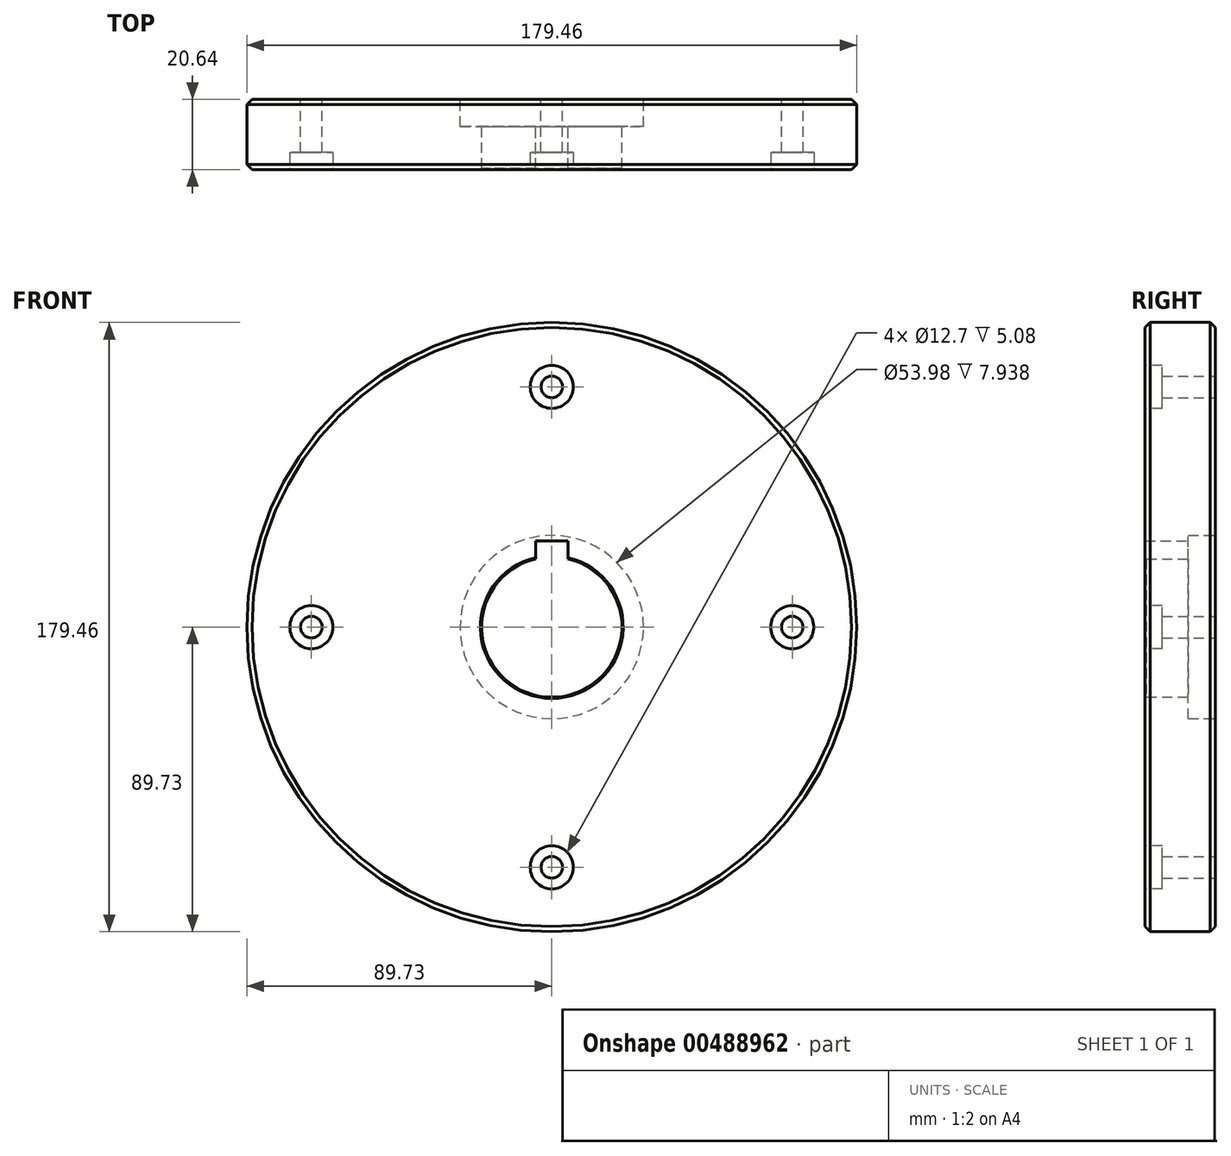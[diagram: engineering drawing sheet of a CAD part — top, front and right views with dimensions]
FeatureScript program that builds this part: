
annotation { "Feature Type Name" : "Feature", "Feature Type Description" : "" }
export const myFeature = defineFeature(function(context is Context, id is Id, definition is map)
    precondition{}
    {
        {
            var Q0;
            Q0=qCreatedBy(makeId("Front.planeOp"),FACE);
            var sketch = newSketch(context, id + "F0", { "sketchPlane" : qUnion([Q0])});
            skCircle(sketch, "E0", {"center": v(0, 0) * mm, "radius": 89.73 * mm});
            skArc(sketch, "E1", {"start": v(-4.76, 20.08) * mm, "mid": v(0, -20.64) * mm, "end": v(4.76, 20.08) * mm});
            skCircle(sketch, "E2", {"center": v(0, 0) * mm, "radius": 26.99 * mm});
            skLineSegment(sketch, "E3", {"start": v(-4.76, 20.08) * mm, "end": v(-4.76, 25.4) * mm});
            skLineSegment(sketch, "E4", {"start": v(-4.76, 25.4) * mm, "end": v(4.76, 25.4) * mm});
            skLineSegment(sketch, "E5", {"start": v(4.76, 25.4) * mm, "end": v(4.76, 20.08) * mm});
            skCircle(sketch, "E6", {"center": v(0, 0) * mm, "radius": 70.75 * mm, "construction": true});
            skCircle(sketch, "E7", {"center": v(0, 70.75) * mm, "radius": 3.18 * mm});
            skCircle(sketch, "E8.1.0", {"center": v(-70.75, 0) * mm, "radius": 3.18 * mm});
            skCircle(sketch, "E8.2.0", {"center": v(0, -70.75) * mm, "radius": 3.18 * mm});
            skCircle(sketch, "E8.3.0", {"center": v(70.75, 0) * mm, "radius": 3.18 * mm});
            skSolve(sketch);
        }
        {
            var Q0;
            Q0=makeQuery(id+"F0.imprint","IMPRINT",FACE,{"disambiguationData":[TD([[makeQuery(id+"F0.imprint","IMPRINT",EDGE,{"derivedFrom":sQuery(id+"F0.wireOp",EDGE,"E0")}),1.0]])]});
            var Q1;
            Q1=makeQuery(id+"F0.imprint","IMPRINT",FACE,{"disambiguationData":[TD([[makeQuery(id+"F0.imprint","IMPRINT",EDGE,{"derivedFrom":sQuery(id+"F0.wireOp",EDGE,"E1")}),-1.0]])]});
            extrude(context, id + "F1", {"entities" : qUnion([Q0, Q1]), "depth" : 20.64 * mm});
        }
        {
            var Q0;
            Q0=makeQuery(id+"F0.imprint","IMPRINT",FACE,{"disambiguationData":[TD([[makeQuery(id+"F0.imprint","IMPRINT",EDGE,{"derivedFrom":sQuery(id+"F0.wireOp",EDGE,"E1")}),-1.0]])]});
            extrude(context, id + "F2", {"entities" : qUnion([Q0]), "operationType" : NewBodyOperationType.REMOVE, "depth" : 7.94 * mm});
        }
        {
            var Q0;
            Q0=makeQuery(id+"F1.opExtrude","CAP_FACE",FACE,{"disambiguationData":[OSD([sQuery(id+"F0.wireOp",EDGE,"E0"),sQuery(id+"F0.wireOp",EDGE,"E1"),sQuery(id+"F0.wireOp",EDGE,"E3"),sQuery(id+"F0.wireOp",EDGE,"E4"),sQuery(id+"F0.wireOp",EDGE,"E5"),sQuery(id+"F0.wireOp",EDGE,"E7"),sQuery(id+"F0.wireOp",EDGE,"E8.1.0"),sQuery(id+"F0.wireOp",EDGE,"E8.2.0"),sQuery(id+"F0.wireOp",EDGE,"E8.3.0")])],"isStart":false});
            var sketch = newSketch(context, id + "F3", { "sketchPlane" : qUnion([Q0])});
            skCircle(sketch, "E9", {"center": v(0, 70.75) * mm, "radius": 6.35 * mm});
            skCircle(sketch, "E10.1.0", {"center": v(-70.75, 0) * mm, "radius": 6.35 * mm});
            skCircle(sketch, "E10.2.0", {"center": v(0, -70.75) * mm, "radius": 6.35 * mm});
            skCircle(sketch, "E10.3.0", {"center": v(70.75, 0) * mm, "radius": 6.35 * mm});
            skPoint(sketch, "E10.center", {"position": v(0, 0) * mm});
            skSolve(sketch);
        }
        {
            var Q0;
            Q0=makeQuery(id+"F3.imprint","IMPRINT",FACE,{"disambiguationData":[TD([[makeQuery(id+"F3.imprint","IMPRINT",EDGE,{"derivedFrom":sQuery(id+"F3.wireOp",EDGE,"E9")}),1.0]])]});
            var Q1;
            Q1=makeQuery(id+"F3.imprint","IMPRINT",FACE,{"disambiguationData":[TD([[makeQuery(id+"F3.imprint","IMPRINT",EDGE,{"derivedFrom":sQuery(id+"F3.wireOp",EDGE,"E10.1.0")}),1.0]])]});
            var Q2;
            Q2=makeQuery(id+"F3.imprint","IMPRINT",FACE,{"disambiguationData":[TD([[makeQuery(id+"F3.imprint","IMPRINT",EDGE,{"derivedFrom":sQuery(id+"F3.wireOp",EDGE,"E10.2.0")}),1.0]])]});
            var Q3;
            Q3=makeQuery(id+"F3.imprint","IMPRINT",FACE,{"disambiguationData":[TD([[makeQuery(id+"F3.imprint","IMPRINT",EDGE,{"derivedFrom":sQuery(id+"F3.wireOp",EDGE,"E10.3.0")}),1.0]])]});
            extrude(context, id + "F4", {"entities" : qUnion([Q0, Q1, Q2, Q3]), "operationType" : NewBodyOperationType.REMOVE, "oppositeDirection" : true, "depth" : 5.08 * mm});
        }
        {
            var Q0;
            Q0=makeQuery(id+"F1.opExtrude","SWEPT_FACE",FACE,{"disambiguationData":[OSD([sQuery(id+"F0.wireOp",EDGE,"E0")])]});
            chamfer(context, id + "F5", {"entities" : qUnion([Q0]), "width" : 1.52 * mm, "tangentPropagation" : true});
        }
        {
            var Q0;
            Q0=makeQuery(id+"F1.opExtrude","CAP_EDGE",EDGE,{"disambiguationData":[OSD([sQuery(id+"F0.wireOp",EDGE,"E1")])],"isStart":false});
            var Q1;
            Q1=makeQuery(id+"F4.boolean.opBoolean","COPY",EDGE,{"derivedFrom":makeQuery(id+"F4.opExtrude","CAP_EDGE",EDGE,{"disambiguationData":[OSD([sQuery(id+"F3.wireOp",EDGE,"E10.1.0")])],"isStart":true})});
            var Q2;
            Q2=makeQuery(id+"F4.boolean.opBoolean","COPY",EDGE,{"derivedFrom":makeQuery(id+"F4.opExtrude","CAP_EDGE",EDGE,{"disambiguationData":[OSD([sQuery(id+"F3.wireOp",EDGE,"E9")])],"isStart":true})});
            var Q3;
            Q3=makeQuery(id+"F4.boolean.opBoolean","COPY",EDGE,{"derivedFrom":makeQuery(id+"F4.opExtrude","CAP_EDGE",EDGE,{"disambiguationData":[OSD([sQuery(id+"F3.wireOp",EDGE,"E10.3.0")])],"isStart":true})});
            var Q4;
            Q4=makeQuery(id+"F4.boolean.opBoolean","COPY",EDGE,{"derivedFrom":makeQuery(id+"F4.opExtrude","CAP_EDGE",EDGE,{"disambiguationData":[OSD([sQuery(id+"F3.wireOp",EDGE,"E10.2.0")])],"isStart":true})});
            var Q5;
            Q5=makeQuery(id+"F2.boolean.opBoolean","COPY",EDGE,{"derivedFrom":makeQuery(id+"F2.opExtrude","CAP_EDGE",EDGE,{"disambiguationData":[OSD([sQuery(id+"F0.wireOp",EDGE,"E1")])],"isStart":false})});
            chamfer(context, id + "F6", {"entities" : qUnion([Q0, Q1, Q2, Q3, Q4, Q5]), "width" : 0.38 * mm, "tangentPropagation" : true});
        }
    });
